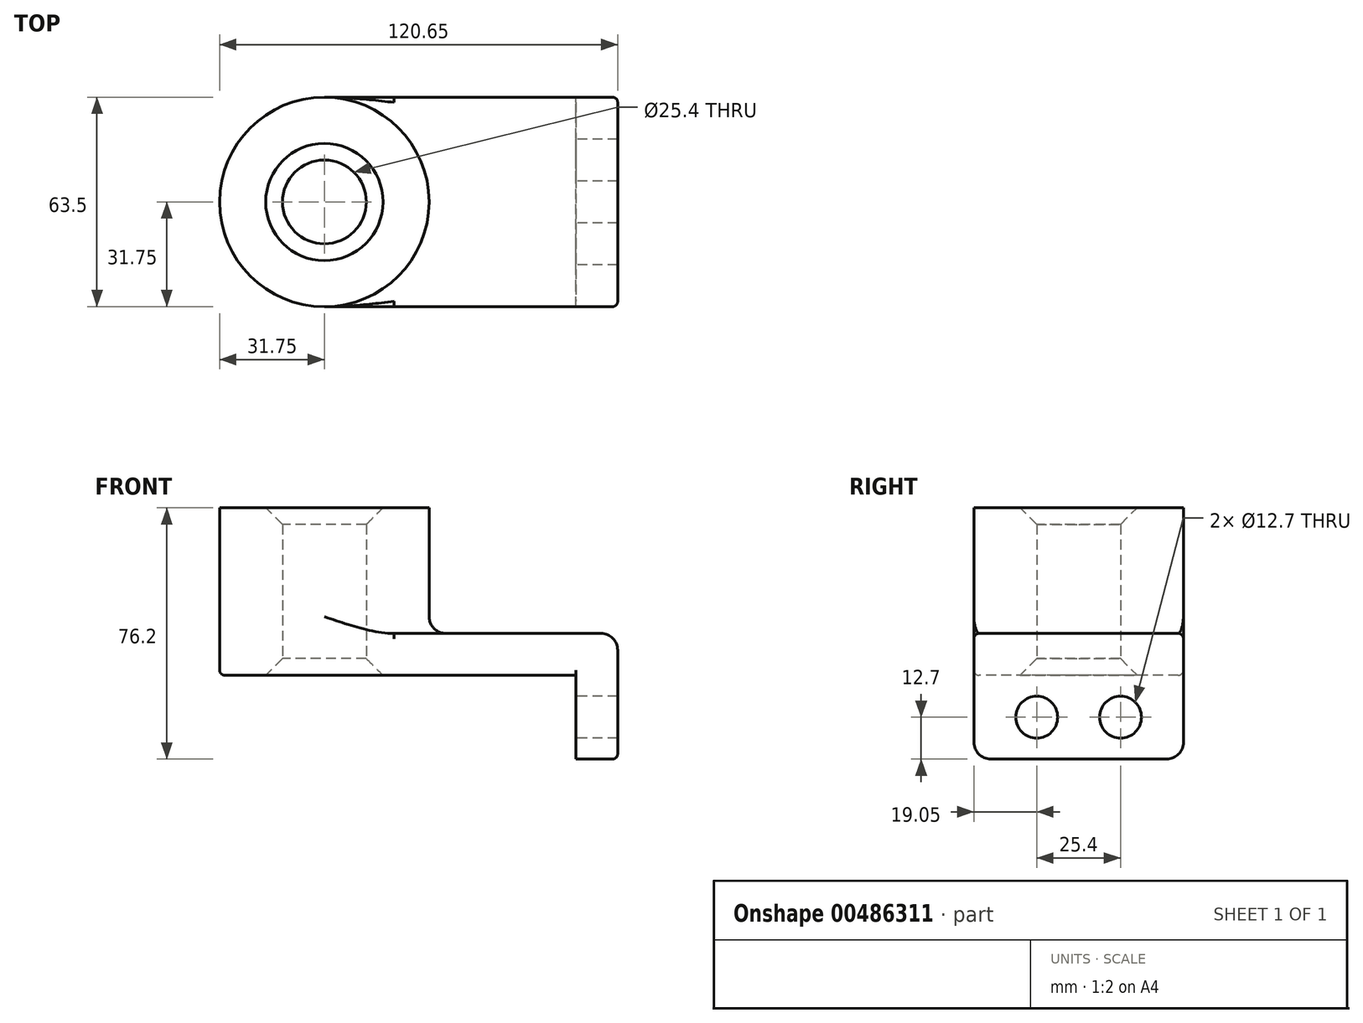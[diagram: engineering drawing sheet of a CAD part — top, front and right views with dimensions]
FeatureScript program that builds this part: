
annotation { "Feature Type Name" : "Feature", "Feature Type Description" : "" }
export const myFeature = defineFeature(function(context is Context, id is Id, definition is map)
    precondition{}
    {
        {
            var Q0;
            Q0=qCreatedBy(makeId("Top.planeOp"),FACE);
            var sketch = newSketch(context, id + "F0", { "sketchPlane" : qUnion([Q0])});
            skLineSegment(sketch, "E0.bottom", {"start": v(38.1, 31.75) * mm, "end": v(-38.1, 31.75) * mm});
            skLineSegment(sketch, "E0.top", {"start": v(38.1, -31.75) * mm, "end": v(-38.1, -31.75) * mm});
            skLineSegment(sketch, "E0.left", {"start": v(38.1, 31.75) * mm, "end": v(38.1, -31.75) * mm});
            skLineSegment(sketch, "E0.right", {"start": v(-38.1, 31.75) * mm, "end": v(-38.1, -31.75) * mm});
            skPoint(sketch, "E0.middle", {"position": v(0, 0) * mm});
            skCircle(sketch, "E1", {"center": v(-38.1, 0) * mm, "radius": 31.75 * mm});
            skCircle(sketch, "E2", {"center": v(-38.1, 0) * mm, "radius": 12.7 * mm});
            skSolve(sketch);
        }
        {
            var Q0;
            Q0 = qSketchRegion(id + "F0", true);
            extrude(context, id + "F1", {"entities" : qUnion([Q0]), "depth" : 12.7 * mm});
        }
        {
            var Q0;
            {var subQ1=sQuery(id+"F0.wireOp",EDGE,"E0.right");var subQ3=sQuery(id+"F0.wireOp",EDGE,"E2");var subQ4=makeQuery(id+"F0.imprint","INTERSECT",VERTEX,{"disambiguationData":[OD(0.0)],"derivedFrom":[subQ1,subQ3]});Q0=makeQuery(id+"F0.imprint","IMPRINT",FACE,{"disambiguationData":[TD([[makeQuery(id+"F0.imprint","IMPRINT",EDGE,{"disambiguationData":[TD([[subQ4,-1.0]])],"derivedFrom":subQ3}),-1.0]])]});}
            var Q1;
            {var subQ1=sQuery(id+"F0.wireOp",EDGE,"E0.right");var subQ3=sQuery(id+"F0.wireOp",EDGE,"E2");var subQ4=makeQuery(id+"F0.imprint","INTERSECT",VERTEX,{"disambiguationData":[OD(0.0)],"derivedFrom":[subQ1,subQ3]});Q1=makeQuery(id+"F0.imprint","IMPRINT",FACE,{"disambiguationData":[TD([[makeQuery(id+"F0.imprint","IMPRINT",EDGE,{"disambiguationData":[TD([[subQ4,1.0]])],"derivedFrom":subQ3}),-1.0]])]});}
            extrude(context, id + "F2", {"entities" : qUnion([Q0, Q1]), "operationType" : NewBodyOperationType.ADD, "depth" : 50.8 * mm});
        }
        {
            var Q0;
            Q0=makeQuery(id+"F1.opExtrude","SWEPT_FACE",FACE,{"disambiguationData":[OSD([sQuery(id+"F0.wireOp",EDGE,"E0.left")])]});
            var sketch = newSketch(context, id + "F3", { "sketchPlane" : qUnion([Q0])});
            skLineSegment(sketch, "E3.bottom", {"start": v(-31.75, 12.7) * mm, "end": v(31.75, 12.7) * mm});
            skLineSegment(sketch, "E3.top", {"start": v(-31.75, -25.4) * mm, "end": v(31.75, -25.4) * mm});
            skLineSegment(sketch, "E3.left", {"start": v(-31.75, 12.7) * mm, "end": v(-31.75, -25.4) * mm});
            skLineSegment(sketch, "E3.right", {"start": v(31.75, 12.7) * mm, "end": v(31.75, -25.4) * mm});
            skCircle(sketch, "E4", {"center": v(-12.7, -12.7) * mm, "radius": 6.35 * mm});
            skLineSegment(sketch, "E5", {"start": v(0, 0) * mm, "end": v(0, -25.4) * mm});
            skCircle(sketch, "E6.MirrorC", {"center": v(12.7, -12.7) * mm, "radius": 6.35 * mm});
            skSolve(sketch);
        }
        {
            var Q0;
            Q0 = qSketchRegion(id + "F3", true);
            extrude(context, id + "F4", {"entities" : qUnion([Q0]), "operationType" : NewBodyOperationType.ADD, "depth" : 12.7 * mm});
        }
        {
            var Q0;
            {var subQ0=sQuery(id+"F0.wireOp",EDGE,"E1");Q0=makeQuery(id+"F2.boolean.opBoolean","INTERSECT",EDGE,{"derivedFrom":[makeQuery(id+"F1.opExtrude","CAP_FACE",FACE,{"disambiguationData":[OSD([sQuery(id+"F0.wireOp",EDGE,"E0.bottom"),sQuery(id+"F0.wireOp",EDGE,"E0.top"),sQuery(id+"F0.wireOp",EDGE,"E0.left"),subQ0,sQuery(id+"F0.wireOp",EDGE,"E2")])],"isStart":false}),makeQuery(id+"F2.opExtrude","SWEPT_FACE",FACE,{"disambiguationData":[OSD([subQ0])]})]});}
            var Q1;
            Q1=makeQuery(id+"F4.opExtrude","CAP_EDGE",EDGE,{"disambiguationData":[OSD([sQuery(id+"F3.wireOp",EDGE,"E3.bottom")])],"isStart":false});
            var Q2;
            Q2=makeQuery(id+"F4.opExtrude","SWEPT_EDGE",EDGE,{"disambiguationData":[OSD([sQuery(id+"F3.wireOp",EDGE,"E3.top"),sQuery(id+"F3.wireOp",EDGE,"E3.left")])]});
            var Q3;
            Q3=makeQuery(id+"F4.opExtrude","SWEPT_EDGE",EDGE,{"disambiguationData":[OSD([sQuery(id+"F3.wireOp",EDGE,"E3.top"),sQuery(id+"F3.wireOp",EDGE,"E3.right")])]});
            fillet(context, id + "F5", {"entities" : qUnion([Q0, Q1, Q2, Q3]), "radius" : 5.08 * mm, "tangentPropagation" : true, "allowEdgeOverflow" : false});
        }
        {
            var Q0;
            Q0=makeQuery(id+"F4.boolean.opBoolean","MERGE",EDGE,{"derivedFrom":[makeQuery(id+"F1.opExtrude","CAP_EDGE",EDGE,{"disambiguationData":[OSD([sQuery(id+"F0.wireOp",EDGE,"E0.top")])],"isStart":false}),makeQuery(id+"F4.opExtrude","SWEPT_EDGE",EDGE,{"disambiguationData":[OSD([sQuery(id+"F3.wireOp",EDGE,"E3.bottom"),sQuery(id+"F3.wireOp",EDGE,"E3.left")])]})]});
            var Q1;
            Q1=makeQuery(id+"F1.opExtrude","CAP_EDGE",EDGE,{"disambiguationData":[OSD([sQuery(id+"F0.wireOp",EDGE,"E0.top")])],"isStart":true});
            var Q2;
            Q2=makeQuery(id+"F1.opExtrude","CAP_EDGE",EDGE,{"disambiguationData":[OSD([sQuery(id+"F0.wireOp",EDGE,"E0.left")])],"isStart":true});
            fillet(context, id + "F6", {"entities" : qUnion([Q0, Q1, Q2]), "radius" : 1.59 * mm, "tangentPropagation" : true, "allowEdgeOverflow" : false});
        }
        {
            var Q0;
            {var subQ0=sQuery(id+"F0.wireOp",EDGE,"E2");Q0=makeQuery(id+"F2.boolean.opBoolean","MERGE",FACE,{"derivedFrom":[makeQuery(id+"F1.opExtrude","SWEPT_FACE",FACE,{"disambiguationData":[OSD([subQ0])]}),makeQuery(id+"F2.opExtrude","SWEPT_FACE",FACE,{"disambiguationData":[OSD([subQ0])]})]});}
            chamfer(context, id + "F7", {"entities" : qUnion([Q0]), "width" : 5.08 * mm, "tangentPropagation" : true});
        }
    });
